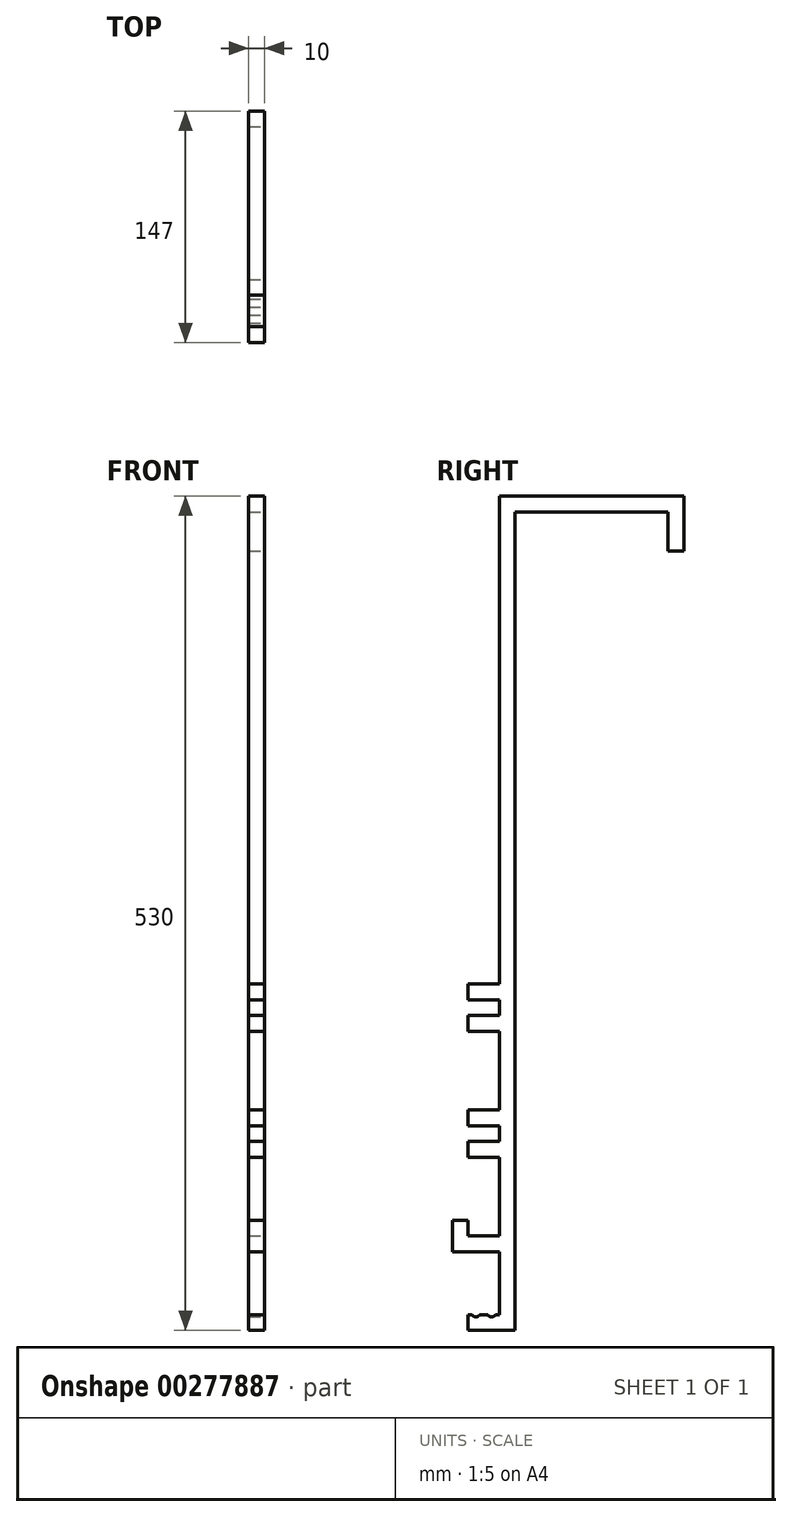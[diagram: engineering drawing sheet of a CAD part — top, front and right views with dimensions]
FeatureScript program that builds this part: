
annotation { "Feature Type Name" : "Feature", "Feature Type Description" : "" }
export const myFeature = defineFeature(function(context is Context, id is Id, definition is map)
    precondition{}
    {
        {
            var Q0;
            Q0=qCreatedBy(makeId("Right.planeOp"),FACE);
            var sketch = newSketch(context, id + "F0", { "sketchPlane" : qUnion([Q0])});
            skLineSegment(sketch, "E0", {"start": v(-1.6, 316.93) * mm, "end": v(-1.6, 6.93) * mm});
            skLineSegment(sketch, "E1", {"start": v(-1.6, 6.93) * mm, "end": v(-21.6, 6.93) * mm});
            skLineSegment(sketch, "E2", {"start": v(-21.6, 6.93) * mm, "end": v(-21.6, -3.07) * mm});
            skLineSegment(sketch, "E3", {"start": v(-21.6, -3.07) * mm, "end": v(-1.6, -3.07) * mm});
            skLineSegment(sketch, "E4", {"start": v(-1.6, -3.07) * mm, "end": v(-1.6, -13.07) * mm});
            skLineSegment(sketch, "E5", {"start": v(-1.6, -13.07) * mm, "end": v(-21.6, -13.07) * mm});
            skLineSegment(sketch, "E6", {"start": v(-21.6, -13.07) * mm, "end": v(-21.6, -23.07) * mm});
            skLineSegment(sketch, "E7", {"start": v(-21.6, -23.07) * mm, "end": v(-1.6, -23.07) * mm});
            skLineSegment(sketch, "E8", {"start": v(-1.6, -23.07) * mm, "end": v(-1.6, -73.07) * mm});
            skLineSegment(sketch, "E9", {"start": v(-1.6, -73.07) * mm, "end": v(-21.6, -73.07) * mm});
            skLineSegment(sketch, "E10", {"start": v(-21.6, -73.07) * mm, "end": v(-21.6, -83.07) * mm});
            skLineSegment(sketch, "E11", {"start": v(-21.6, -83.07) * mm, "end": v(-1.6, -83.07) * mm});
            skLineSegment(sketch, "E12", {"start": v(-1.6, -83.07) * mm, "end": v(-1.6, -93.07) * mm});
            skLineSegment(sketch, "E13", {"start": v(-1.6, -93.07) * mm, "end": v(-21.6, -93.07) * mm});
            skLineSegment(sketch, "E14", {"start": v(-21.6, -93.07) * mm, "end": v(-21.6, -103.07) * mm});
            skLineSegment(sketch, "E15", {"start": v(-21.6, -103.07) * mm, "end": v(-1.6, -103.07) * mm});
            skLineSegment(sketch, "E16", {"start": v(-1.6, -103.07) * mm, "end": v(-1.6, -153.07) * mm});
            skLineSegment(sketch, "E17", {"start": v(-1.6, -153.07) * mm, "end": v(-21.6, -153.07) * mm});
            skLineSegment(sketch, "E18", {"start": v(-21.6, -153.07) * mm, "end": v(-21.6, -143.07) * mm});
            skLineSegment(sketch, "E19", {"start": v(-21.6, -143.07) * mm, "end": v(-31.6, -143.07) * mm});
            skLineSegment(sketch, "E20", {"start": v(-31.6, -143.07) * mm, "end": v(-31.6, -163.07) * mm});
            skLineSegment(sketch, "E21", {"start": v(-31.6, -163.07) * mm, "end": v(-1.6, -163.07) * mm});
            skLineSegment(sketch, "E22", {"start": v(-1.6, -163.07) * mm, "end": v(-1.6, -203.07) * mm});
            skLineSegment(sketch, "E23", {"start": v(-21.6, -203.07) * mm, "end": v(-21.6, -213.07) * mm});
            skLineSegment(sketch, "E24", {"start": v(-21.6, -213.07) * mm, "end": v(8.4, -213.07) * mm});
            skLineSegment(sketch, "E25", {"start": v(-1.6, -203.07) * mm, "end": v(-4.1, -203.07) * mm});
            skLineSegment(sketch, "E26", {"start": v(-9.1, -203.07) * mm, "end": v(-14.1, -203.07) * mm});
            skLineSegment(sketch, "E27", {"start": v(-19.1, -203.07) * mm, "end": v(-21.6, -203.07) * mm});
            skArc(sketch, "E28", {"start": v(-9.1, -203.07) * mm, "mid": v(-6.6, -204.42) * mm, "end": v(-4.1, -203.07) * mm});
            skArc(sketch, "E29", {"start": v(-19.1, -203.07) * mm, "mid": v(-16.6, -204.42) * mm, "end": v(-14.1, -203.07) * mm});
            skLineSegment(sketch, "E30", {"start": v(-1.6, 316.93) * mm, "end": v(115.4, 316.93) * mm});
            skLineSegment(sketch, "E31", {"start": v(115.4, 316.93) * mm, "end": v(115.4, 281.93) * mm});
            skLineSegment(sketch, "E32", {"start": v(115.4, 281.93) * mm, "end": v(105.4, 281.93) * mm});
            skLineSegment(sketch, "E33", {"start": v(105.4, 281.93) * mm, "end": v(105.4, 306.93) * mm});
            skLineSegment(sketch, "E34", {"start": v(105.4, 306.93) * mm, "end": v(8.4, 306.93) * mm});
            skLineSegment(sketch, "E35", {"start": v(8.4, 306.93) * mm, "end": v(8.4, -213.07) * mm});
            skSolve(sketch);
        }
        {
            var Q0;
            Q0 = qSketchRegion(id + "F0", true);
            extrude(context, id + "F1", {"entities" : qUnion([Q0]), "oppositeDirection" : true, "depth" : 10 * mm});
        }
    });
